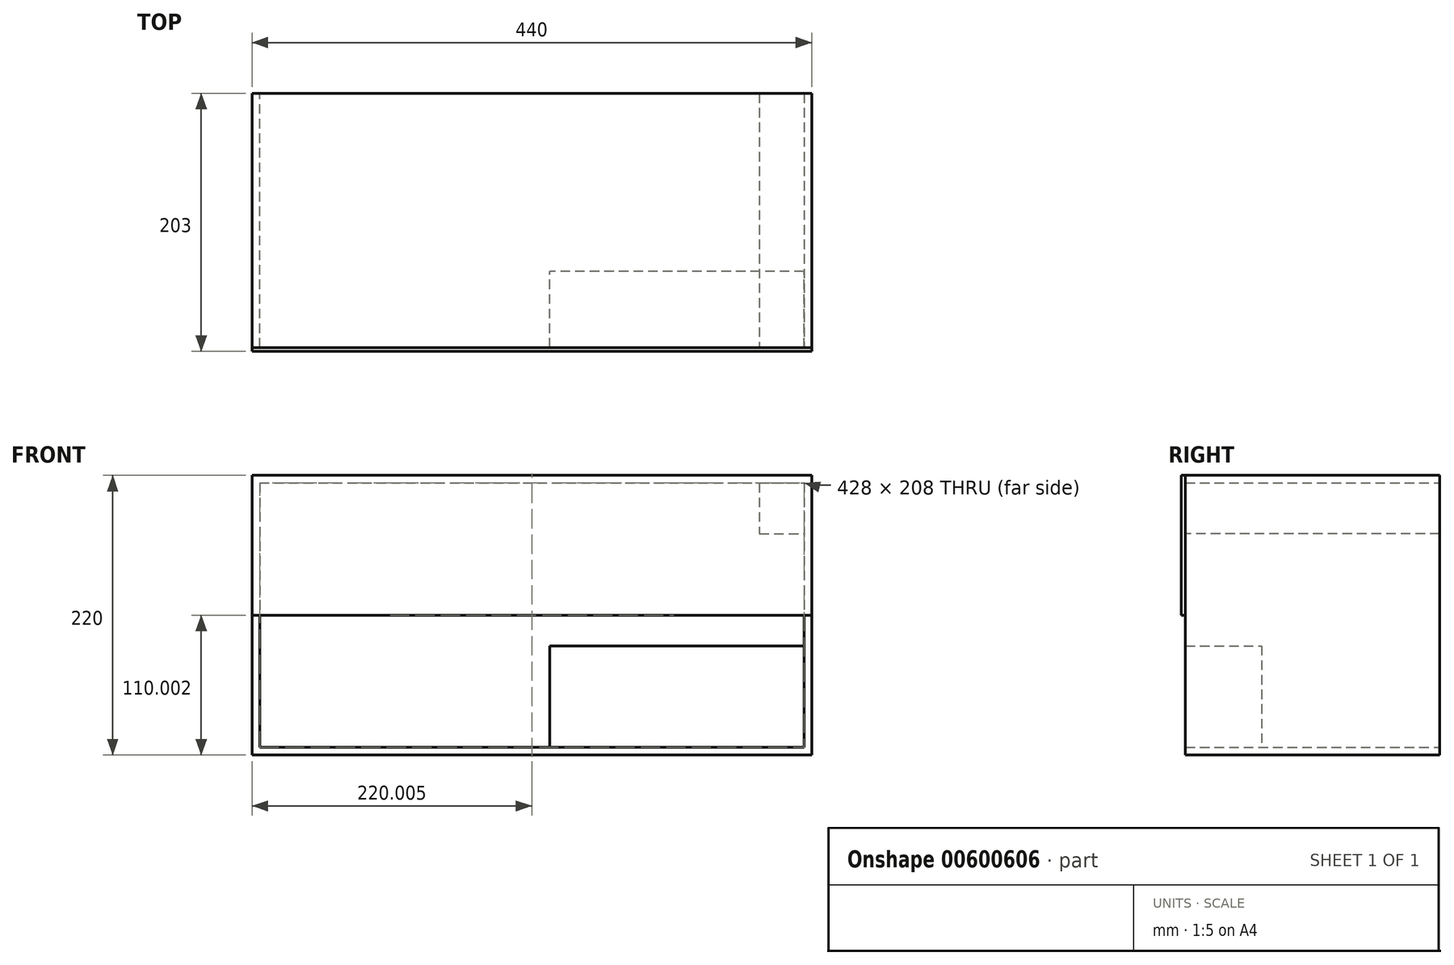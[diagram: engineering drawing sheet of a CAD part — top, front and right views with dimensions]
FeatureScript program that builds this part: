
annotation { "Feature Type Name" : "Feature", "Feature Type Description" : "" }
export const myFeature = defineFeature(function(context is Context, id is Id, definition is map)
    precondition{}
    {
        {
            var Q0;
            Q0=qCreatedBy(makeId("Front.planeOp"),FACE);
            var sketch = newSketch(context, id + "F0", { "sketchPlane" : qUnion([Q0])});
            skLineSegment(sketch, "E0.bottom", {"start": v(-203.14, 77.6) * mm, "end": v(236.86, 77.6) * mm});
            skLineSegment(sketch, "E0.top", {"start": v(-203.14, -142.4) * mm, "end": v(236.86, -142.4) * mm});
            skLineSegment(sketch, "E0.left", {"start": v(-203.14, 77.6) * mm, "end": v(-203.14, -142.4) * mm});
            skLineSegment(sketch, "E0.right", {"start": v(236.86, 77.6) * mm, "end": v(236.86, -142.4) * mm});
            skLineSegment(sketch, "E1.0", {"start": v(-197.14, 71.6) * mm, "end": v(230.86, 71.6) * mm});
            skLineSegment(sketch, "E1.1", {"start": v(-197.14, 71.6) * mm, "end": v(-197.14, -136.4) * mm});
            skLineSegment(sketch, "E1.2", {"start": v(-197.14, -136.4) * mm, "end": v(230.86, -136.4) * mm});
            skLineSegment(sketch, "E1.3", {"start": v(230.86, 71.6) * mm, "end": v(230.86, -136.4) * mm});
            skSolve(sketch);
        }
        {
            var Q0;
            Q0=makeQuery(id+"F0.imprint","IMPRINT",FACE,{"disambiguationData":[TD([[makeQuery(id+"F0.imprint","IMPRINT",EDGE,{"derivedFrom":sQuery(id+"F0.wireOp",EDGE,"E0.bottom")}),-1.0]])]});
            extrude(context, id + "F1", {"entities" : qUnion([Q0]), "endBound" : BoundingType.SYMMETRIC, "depth" : 200 * mm, "offsetDistance" : 25 * mm});
        }
        {
            var Q0;
            Q0=makeQuery(id+"F1.opExtrude","CAP_FACE",FACE,{"disambiguationData":[OSD([sQuery(id+"F0.wireOp",EDGE,"E0.bottom"),sQuery(id+"F0.wireOp",EDGE,"E0.top"),sQuery(id+"F0.wireOp",EDGE,"E0.left"),sQuery(id+"F0.wireOp",EDGE,"E0.right"),sQuery(id+"F0.wireOp",EDGE,"E1.0"),sQuery(id+"F0.wireOp",EDGE,"E1.1"),sQuery(id+"F0.wireOp",EDGE,"E1.2"),sQuery(id+"F0.wireOp",EDGE,"E1.3")])],"isStart":false});
            var sketch = newSketch(context, id + "F2", { "sketchPlane" : qUnion([Q0])});
            skLineSegment(sketch, "E2.bottom", {"start": v(-203.14, 77.6) * mm, "end": v(236.86, 77.6) * mm});
            skLineSegment(sketch, "E2.top", {"start": v(-203.14, -32.4) * mm, "end": v(236.86, -32.4) * mm});
            skLineSegment(sketch, "E2.left", {"start": v(-203.14, 77.6) * mm, "end": v(-203.14, -32.4) * mm});
            skLineSegment(sketch, "E2.right", {"start": v(236.86, 77.6) * mm, "end": v(236.86, -32.4) * mm});
            skSolve(sketch);
        }
        {
            var Q0;
            Q0=makeQuery(id+"F2.imprint","IMPRINT",FACE,{"disambiguationData":[TD([[makeQuery(id+"F2.imprint","IMPRINT",EDGE,{"derivedFrom":sQuery(id+"F2.wireOp",EDGE,"E2.bottom")}),-1.0]])]});
            var Q1;
            {var subQ5=makeQuery(id+"F1.opExtrude","CAP_EDGE",EDGE,{"disambiguationData":[OSD([sQuery(id+"F0.wireOp",EDGE,"E1.0")])],"isStart":false});Q1=makeQuery(id+"F2.imprint","IMPRINT",FACE,{"disambiguationData":[TD([[makeQuery(id+"F2.imprint","IMPRINT",EDGE,{"derivedFrom":subQ5}),-1.0]])]});}
            extrude(context, id + "F3", {"entities" : qUnion([Q0, Q1]), "depth" : 3 * mm, "offsetDistance" : 25 * mm});
        }
        {
            var Q0;
            Q0=makeQuery(id+"F1.opExtrude","SWEPT_FACE",FACE,{"disambiguationData":[OSD([sQuery(id+"F0.wireOp",EDGE,"E1.2")])]});
            var sketch = newSketch(context, id + "F4", { "sketchPlane" : qUnion([Q0])});
            skLineSegment(sketch, "E3.bottom", {"start": v(230.86, -100) * mm, "end": v(30.86, -100) * mm});
            skLineSegment(sketch, "E3.top", {"start": v(230.86, -40) * mm, "end": v(30.86, -40) * mm});
            skLineSegment(sketch, "E3.left", {"start": v(230.86, -100) * mm, "end": v(230.86, -40) * mm});
            skLineSegment(sketch, "E3.right", {"start": v(30.86, -100) * mm, "end": v(30.86, -40) * mm});
            skLineSegment(sketch, "E4.bottom", {"start": v(230.86, -40) * mm, "end": v(175.86, -40) * mm});
            skLineSegment(sketch, "E4.top", {"start": v(230.86, 100) * mm, "end": v(175.86, 100) * mm});
            skLineSegment(sketch, "E4.left", {"start": v(230.86, -40) * mm, "end": v(230.86, 100) * mm});
            skLineSegment(sketch, "E4.right", {"start": v(175.86, -40) * mm, "end": v(175.86, 100) * mm});
            skSolve(sketch);
        }
        {
            var Q0;
            Q0=makeQuery(id+"F4.imprint","IMPRINT",FACE,{"disambiguationData":[TD([[makeQuery(id+"F4.imprint","IMPRINT",EDGE,{"derivedFrom":sQuery(id+"F4.wireOp",EDGE,"E4.bottom")}),-1.0]])]});
            var Q1;
            Q1=makeQuery(id+"F4.imprint","IMPRINT",FACE,{"disambiguationData":[TD([[makeQuery(id+"F4.imprint","IMPRINT",EDGE,{"derivedFrom":sQuery(id+"F4.wireOp",EDGE,"E3.bottom")}),1.0]])]});
            extrude(context, id + "F5", {"entities" : qUnion([Q0, Q1]), "depth" : 80 * mm, "offsetDistance" : 25 * mm});
        }
        {
            var Q0;
            Q0=makeQuery(id+"F1.opExtrude","SWEPT_FACE",FACE,{"disambiguationData":[OSD([sQuery(id+"F0.wireOp",EDGE,"E1.3")])]});
            var sketch = newSketch(context, id + "F6", { "sketchPlane" : qUnion([Q0])});
            skLineSegment(sketch, "E5.bottom", {"start": v(-100, 71.6) * mm, "end": v(100, 71.6) * mm});
            skLineSegment(sketch, "E5.top", {"start": v(-100, 31.6) * mm, "end": v(100, 31.6) * mm});
            skLineSegment(sketch, "E5.left", {"start": v(-100, 71.6) * mm, "end": v(-100, 31.6) * mm});
            skLineSegment(sketch, "E5.right", {"start": v(100, 71.6) * mm, "end": v(100, 31.6) * mm});
            skSolve(sketch);
        }
        {
            var Q0;
            Q0=makeQuery(id+"F6.imprint","IMPRINT",FACE,{"disambiguationData":[TD([[makeQuery(id+"F6.imprint","IMPRINT",EDGE,{"derivedFrom":sQuery(id+"F6.wireOp",EDGE,"E5.bottom")}),1.0]])]});
            extrude(context, id + "F7", {"entities" : qUnion([Q0]), "depth" : 35 * mm, "offsetDistance" : 25 * mm});
        }
    });
